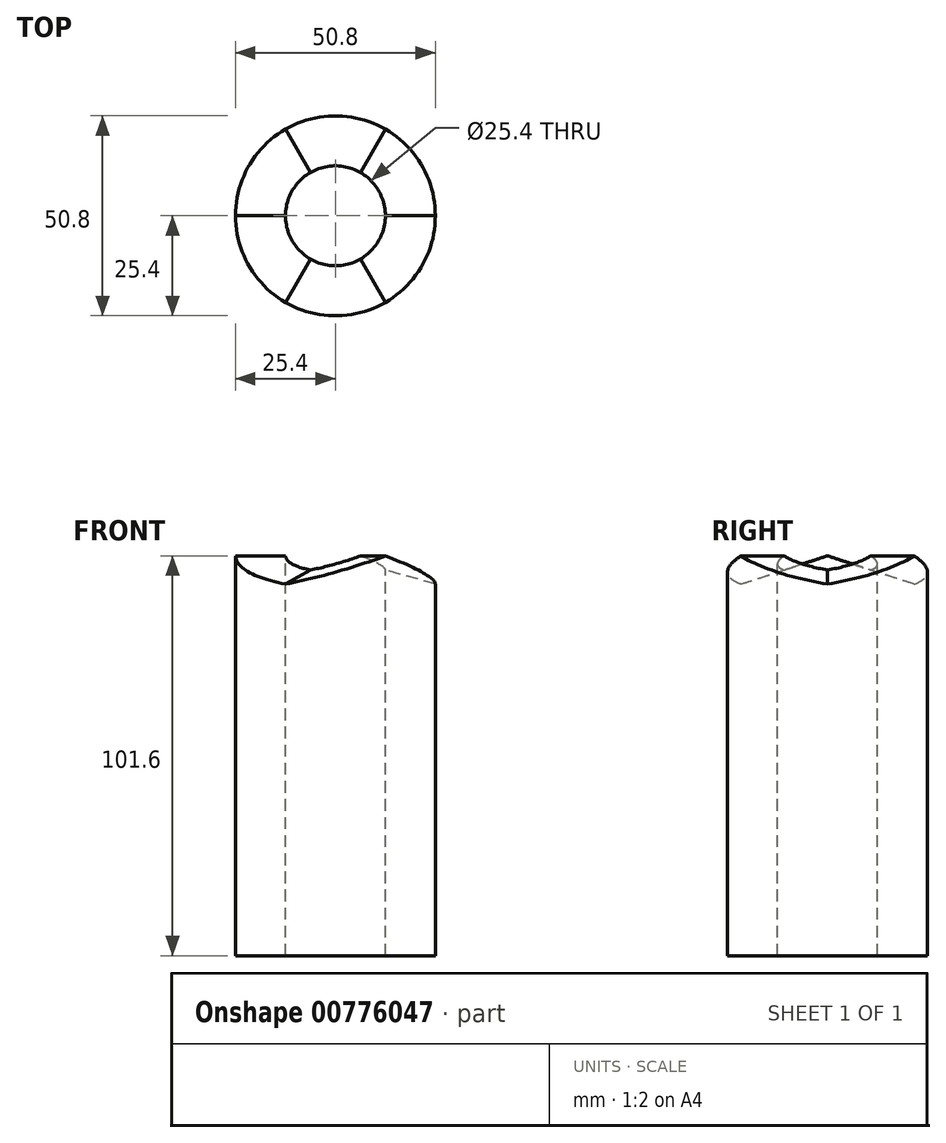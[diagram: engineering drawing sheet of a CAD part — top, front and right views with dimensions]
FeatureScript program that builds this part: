
annotation { "Feature Type Name" : "Feature", "Feature Type Description" : "" }
export const myFeature = defineFeature(function(context is Context, id is Id, definition is map)
    precondition{}
    {
        {
            var Q0;
            Q0=qCreatedBy(makeId("Front.planeOp"),FACE);
            var sketch = newSketch(context, id + "F0", { "sketchPlane" : qUnion([Q0])});
            skLineSegment(sketch, "E0.bottom", {"start": v(0, -50.8) * mm, "end": v(-25.4, -50.8) * mm});
            skLineSegment(sketch, "E0.top", {"start": v(0, 50.8) * mm, "end": v(-25.4, 50.8) * mm});
            skLineSegment(sketch, "E0.left", {"start": v(0, -50.8) * mm, "end": v(0, 50.8) * mm});
            skLineSegment(sketch, "E0.right", {"start": v(-25.4, -50.8) * mm, "end": v(-25.4, 50.8) * mm});
            skPoint(sketch, "E0.middle", {"position": v(-12.7, 0) * mm});
            skSolve(sketch);
        }
        {
            var Q0;
            Q0=qCreatedBy(makeId("Right.planeOp"),FACE);
            var sketch = newSketch(context, id + "F1", { "sketchPlane" : qUnion([Q0])});
            skLineSegment(sketch, "E1", {"start": v(0, 0) * mm, "end": v(0, 50.8) * mm});
            skLineSegment(sketch, "E2", {"start": v(0, 50.8) * mm, "end": v(-25.4, 50.8) * mm});
            skLineSegment(sketch, "E3", {"start": v(-25.4, 50.8) * mm, "end": v(-25.4, 42.5) * mm});
            skLineSegment(sketch, "E4", {"start": v(-25.4, 42.5) * mm, "end": v(0, 50.8) * mm});
            skSolve(sketch);
        }
        {
            var Q0;
            Q0=makeQuery(id+"F0.imprint","IMPRINT",FACE,{"disambiguationData":[TD([[makeQuery(id+"F0.imprint","IMPRINT",EDGE,{"derivedFrom":sQuery(id+"F0.wireOp",EDGE,"E0.bottom")}),-1.0]])]});
            var Q1;
            Q1=sQuery(id+"F0.wireOp",EDGE,"E0.left");
            revolve(context, id + "F2", {"surfaceOperationType" : NewSurfaceOperationType.NEW, "entities" : qUnion([Q0]), "axis" : qUnion([Q1]), "revolveType" : RevolveType.ONE_DIRECTION, "angle" : 60 * degree});
        }
        {
            var Q0;
            Q0=makeQuery(id+"F1.imprint","IMPRINT",FACE,{"disambiguationData":[TD([[makeQuery(id+"F1.imprint","IMPRINT",EDGE,{"derivedFrom":sQuery(id+"F1.wireOp",EDGE,"E2")}),1.0]])]});
            extrude(context, id + "F3", {"entities" : qUnion([Q0]), "operationType" : NewBodyOperationType.REMOVE, "oppositeDirection" : true, "depth" : 30.48 * mm, "offsetDistance" : 25.4 * mm});
        }
        {
            var Q0;
            Q0=makeQuery(id+"F2.opRevolve","SWEPT_BODY",BODY,{"disambiguationData":[OSD([sQuery(id+"F0.wireOp",EDGE,"E0.bottom"),sQuery(id+"F0.wireOp",EDGE,"E0.top"),sQuery(id+"F0.wireOp",EDGE,"E0.left"),sQuery(id+"F0.wireOp",EDGE,"E0.right")])]});
            var Q1;
            Q1=makeQuery(id+"F2.opRevolve","CAP_FACE",FACE,{"disambiguationData":[OSD([sQuery(id+"F0.wireOp",EDGE,"E0.bottom"),sQuery(id+"F0.wireOp",EDGE,"E0.top"),sQuery(id+"F0.wireOp",EDGE,"E0.left"),sQuery(id+"F0.wireOp",EDGE,"E0.right")])],"isStart":false});
            mirror(context, id + "F4", {"entities" : qUnion([Q0]), "mirrorPlane" : qUnion([Q1])});
        }
        {
            var Q0;
            Q0=makeQuery(id+"F4.opPattern","COPY",BODY,{"derivedFrom":makeQuery(id+"F2.opRevolve","SWEPT_BODY",BODY,{"disambiguationData":[OSD([sQuery(id+"F0.wireOp",EDGE,"E0.bottom"),sQuery(id+"F0.wireOp",EDGE,"E0.top"),sQuery(id+"F0.wireOp",EDGE,"E0.left"),sQuery(id+"F0.wireOp",EDGE,"E0.right")])]}),"instanceName":"1"});
            var Q1;
            Q1=makeQuery(id+"F4.opPattern","COPY",FACE,{"derivedFrom":makeQuery(id+"F2.opRevolve","CAP_FACE",FACE,{"disambiguationData":[OSD([sQuery(id+"F0.wireOp",EDGE,"E0.bottom"),sQuery(id+"F0.wireOp",EDGE,"E0.top"),sQuery(id+"F0.wireOp",EDGE,"E0.left"),sQuery(id+"F0.wireOp",EDGE,"E0.right")])],"isStart":true}),"instanceName":"1"});
            mirror(context, id + "F5", {"operationType" : NewBodyOperationType.ADD, "entities" : qUnion([Q0]), "mirrorPlane" : qUnion([Q1])});
        }
        {
            var Q0;
            Q0=makeQuery(id+"F2.opRevolve","SWEPT_BODY",BODY,{"disambiguationData":[OSD([sQuery(id+"F0.wireOp",EDGE,"E0.bottom"),sQuery(id+"F0.wireOp",EDGE,"E0.top"),sQuery(id+"F0.wireOp",EDGE,"E0.left"),sQuery(id+"F0.wireOp",EDGE,"E0.right")])]});
            var Q1;
            Q1=qCreatedBy(makeId("Front.planeOp"),FACE);
            mirror(context, id + "F6", {"operationType" : NewBodyOperationType.ADD, "entities" : qUnion([Q0]), "mirrorPlane" : qUnion([Q1])});
        }
        {
            var Q0;
            Q0=qCreatedBy(makeId("Front.planeOp"),FACE);
            var sketch = newSketch(context, id + "F7", { "sketchPlane" : qUnion([Q0])});
            skLineSegment(sketch, "E5.bottom", {"start": v(0, -50.8) * mm, "end": v(12.7, -50.8) * mm});
            skLineSegment(sketch, "E5.top", {"start": v(0, 50.8) * mm, "end": v(12.7, 50.8) * mm});
            skLineSegment(sketch, "E5.left", {"start": v(0, -50.8) * mm, "end": v(0, 50.8) * mm});
            skLineSegment(sketch, "E5.right", {"start": v(12.7, -50.8) * mm, "end": v(12.7, 50.8) * mm});
            skPoint(sketch, "E5.middle", {"position": v(6.35, 0) * mm});
            skSolve(sketch);
        }
        {
            var Q0;
            Q0=makeQuery(id+"F7.imprint","IMPRINT",FACE,{"disambiguationData":[TD([[makeQuery(id+"F7.imprint","IMPRINT",EDGE,{"derivedFrom":sQuery(id+"F7.wireOp",EDGE,"E5.bottom")}),1.0]])]});
            var Q1;
            Q1=sQuery(id+"F7.wireOp",EDGE,"E5.left");
            revolve(context, id + "F8", {"operationType" : NewBodyOperationType.REMOVE, "surfaceOperationType" : NewSurfaceOperationType.NEW, "entities" : qUnion([Q0]), "axis" : qUnion([Q1]), "revolveType" : RevolveType.FULL, "oppositeDirection" : true});
        }
    });
